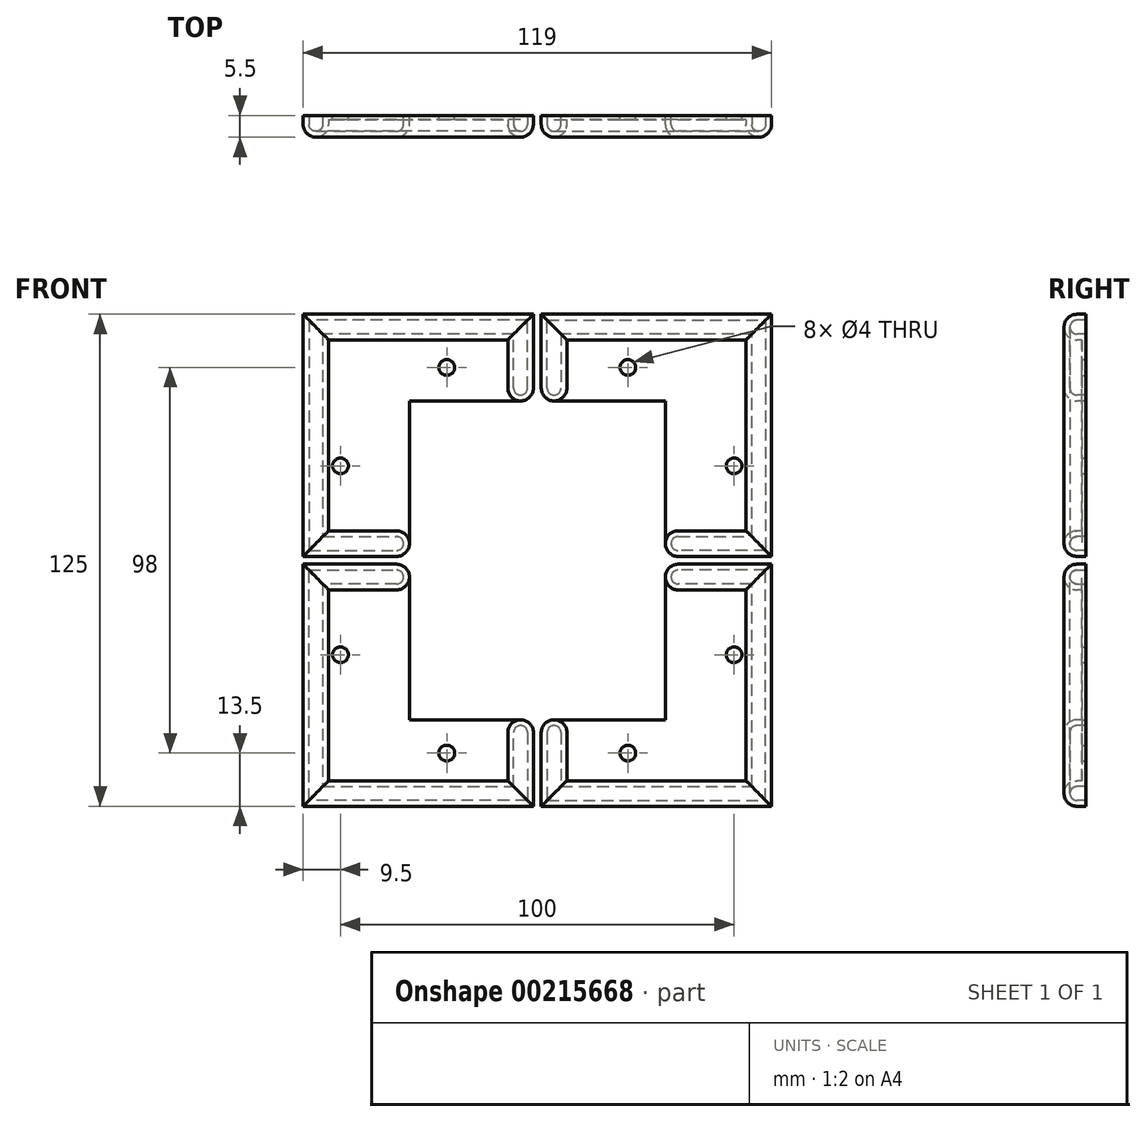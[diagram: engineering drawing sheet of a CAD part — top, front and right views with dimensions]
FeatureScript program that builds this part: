
annotation { "Feature Type Name" : "Feature", "Feature Type Description" : "" }
export const myFeature = defineFeature(function(context is Context, id is Id, definition is map)
    precondition{}
    {
        {
            var Q0;
            Q0=qCreatedBy(makeId("Front.planeOp"),FACE);
            var sketch = newSketch(context, id + "F0", { "sketchPlane" : qUnion([Q0])});
            skLineSegment(sketch, "E0", {"start": v(59.5, 0) * mm, "end": v(59.5, 61.5) * mm});
            skLineSegment(sketch, "E1", {"start": v(59.5, 61.5) * mm, "end": v(1, 61.5) * mm});
            skLineSegment(sketch, "E2", {"start": v(1, 61.5) * mm, "end": v(1, 39.5) * mm});
            skLineSegment(sketch, "E3", {"start": v(1, 39.5) * mm, "end": v(32.5, 39.5) * mm});
            skLineSegment(sketch, "E4", {"start": v(32.5, 39.5) * mm, "end": v(32.5, 0) * mm});
            skLineSegment(sketch, "E5", {"start": v(32.5, 0) * mm, "end": v(59.5, 0) * mm});
            skCircle(sketch, "E6", {"center": v(23, 48) * mm, "radius": 2 * mm});
            skCircle(sketch, "E7", {"center": v(50, 23) * mm, "radius": 2 * mm});
            skSolve(sketch);
        }
        {
            var Q0;
            Q0=qCreatedBy(makeId("Right.planeOp"),FACE);
            var sketch = newSketch(context, id + "F1", { "sketchPlane" : qUnion([Q0])});
            skArc(sketch, "E8", {"start": v(-2.25, 61.5) * mm, "mid": v(-5.5, 58.25) * mm, "end": v(-2.25, 55) * mm});
            skLineSegment(sketch, "E9", {"start": v(0, 61.5) * mm, "end": v(-2.25, 61.5) * mm});
            skLineSegment(sketch, "E10", {"start": v(-2.25, 55) * mm, "end": v(0, 55) * mm});
            skPoint(sketch, "E11", {"position": v(-5.5, 58.25) * mm});
            skLineSegment(sketch, "E12", {"start": v(0, 55) * mm, "end": v(0, 61.5) * mm});
            skSolve(sketch);
        }
        {
            var Q0;
            Q0=qCreatedBy(makeId("Top.planeOp"),FACE);
            cPlane(context, id + "F2", {"entities" : qUnion([Q0]), "cplaneType" : CPlaneType.OFFSET, "offset" : 39.5 * mm, "width" : 150 * mm, "height" : 150 * mm});
        }
        {
            var Q0;
            Q0=qCreatedBy(id+"F2.planeOp",FACE);
            var sketch = newSketch(context, id + "F3", { "sketchPlane" : qUnion([Q0])});
            skArc(sketch, "E13", {"start": v(1, -2.25) * mm, "mid": v(4.25, -5.5) * mm, "end": v(7.5, -2.25) * mm});
            skPoint(sketch, "E14", {"position": v(4.25, -5.5) * mm});
            skPoint(sketch, "E15", {"position": v(1, -2.25) * mm});
            skLineSegment(sketch, "E16", {"start": v(1, 0) * mm, "end": v(7.5, 0) * mm});
            skLineSegment(sketch, "E17", {"start": v(7.5, -2.25) * mm, "end": v(7.5, 0) * mm});
            skLineSegment(sketch, "E18", {"start": v(1, -2.25) * mm, "end": v(1, 0) * mm});
            skSolve(sketch);
        }
        {
            var Q0;
            Q0=makeQuery(id+"F3.imprint","IMPRINT",FACE,{"disambiguationData":[TD([[makeQuery(id+"F3.imprint","IMPRINT",EDGE,{"derivedFrom":sQuery(id+"F3.wireOp",EDGE,"E13")}),1.0]])]});
            var Q1;
            Q1=sQuery(id+"F0.wireOp",EDGE,"E2");
            var Q2;
            Q2=sQuery(id+"F0.wireOp",EDGE,"E1");
            var Q3;
            Q3=sQuery(id+"F0.wireOp",EDGE,"E0");
            var Q4;
            Q4=sQuery(id+"F0.wireOp",EDGE,"E5");
            sweep(context, id + "F4", {"profiles" : qUnion([Q0]), "path" : qUnion([Q1, Q2, Q3, Q4])});
        }
        {
            var Q0;
            Q0 = qSketchRegion(id + "F0", true);
            extrude(context, id + "F5", {"entities" : qUnion([Q0]), "operationType" : NewBodyOperationType.ADD, "depth" : 1 * mm});
        }
        {
            var Q0;
            Q0=makeQuery(id+"F4.opSweep","CAP_EDGE",EDGE,{"disambiguationData":[OSD([sQuery(id+"F0.wireOp",VERTEX,"E2.end"),sQuery(id+"F3.wireOp",EDGE,"E13")])],"isStart":true});
            var Q1;
            Q1=makeQuery(id+"F4.opSweep","CAP_EDGE",EDGE,{"disambiguationData":[OSD([sQuery(id+"F0.wireOp",VERTEX,"E5.start"),sQuery(id+"F3.wireOp",EDGE,"E13")])],"isStart":false});
            fillet(context, id + "F6", {"entities" : qUnion([Q0, Q1]), "radius" : 3.25 * mm, "tangentPropagation" : true, "allowEdgeOverflow" : false});
        }
        {
            var Q0;
            Q0=makeQuery(id+"F4.opSweep","SWEPT_BODY",BODY,{"disambiguationData":[OSD([sQuery(id+"F0.wireOp",EDGE,"E5"),sQuery(id+"F3.wireOp",EDGE,"E13"),sQuery(id+"F3.wireOp",EDGE,"gyNzIB6L-VOB3-YhDV-Oq0C-YqyF9qzvM0NL"),sQuery(id+"F3.wireOp",EDGE,"E16"),sQuery(id+"F3.wireOp",EDGE,"E17")])]});
            var Q1;
            Q1=qCreatedBy(makeId("Right.planeOp"),FACE);
            mirror(context, id + "F7", {"entities" : qUnion([Q0]), "mirrorPlane" : qUnion([Q1])});
        }
        {
            var Q0;
            Q0=qCreatedBy(makeId("Top.planeOp"),FACE);
            cPlane(context, id + "F8", {"entities" : qUnion([Q0]), "cplaneType" : CPlaneType.OFFSET, "offset" : 1 * mm, "oppositeDirection" : true, "width" : 150 * mm, "height" : 150 * mm});
        }
        {
            var Q0;
            Q0=makeQuery(id+"F4.opSweep","SWEPT_BODY",BODY,{"disambiguationData":[OSD([sQuery(id+"F0.wireOp",EDGE,"E5"),sQuery(id+"F3.wireOp",EDGE,"E13"),sQuery(id+"F3.wireOp",EDGE,"E16"),sQuery(id+"F3.wireOp",EDGE,"E17"),sQuery(id+"F3.wireOp",EDGE,"E18")])]});
            var Q1;
            Q1=makeQuery(id+"F7.opPattern","COPY",BODY,{"derivedFrom":makeQuery(id+"F4.opSweep","SWEPT_BODY",BODY,{"disambiguationData":[OSD([sQuery(id+"F0.wireOp",EDGE,"E5"),sQuery(id+"F3.wireOp",EDGE,"E13"),sQuery(id+"F3.wireOp",EDGE,"E16"),sQuery(id+"F3.wireOp",EDGE,"E17"),sQuery(id+"F3.wireOp",EDGE,"E18")])]}),"instanceName":"1"});
            var Q2;
            Q2=qCreatedBy(id+"F8.planeOp",FACE);
            mirror(context, id + "F9", {"entities" : qUnion([Q0, Q1]), "mirrorPlane" : qUnion([Q2])});
        }
        {
            var Q0;
            {var subQ0=sQuery(id+"F0.wireOp",EDGE,"E2");Q0=makeQuery(id+"F7.opPattern","COPY",FACE,{"derivedFrom":makeQuery(id+"F5.boolean.opBoolean","MERGE",FACE,{"derivedFrom":[makeQuery(id+"F4.opSweep","SWEPT_FACE",FACE,{"disambiguationData":[OSD([subQ0,sQuery(id+"F3.wireOp",EDGE,"E16")])]}),makeQuery(id+"F5.opExtrude","CAP_FACE",FACE,{"disambiguationData":[OSD([sQuery(id+"F0.wireOp",EDGE,"E0"),sQuery(id+"F0.wireOp",EDGE,"E1"),subQ0,sQuery(id+"F0.wireOp",EDGE,"E3"),sQuery(id+"F0.wireOp",EDGE,"E4"),sQuery(id+"F0.wireOp",EDGE,"E5"),sQuery(id+"F0.wireOp",EDGE,"E6"),sQuery(id+"F0.wireOp",EDGE,"E7")])],"isStart":true})]}),"instanceName":"1"});}
            var Q1;
            {var subQ0=sQuery(id+"F0.wireOp",EDGE,"E2");Q1=makeQuery(id+"F9.opPattern","COPY",FACE,{"derivedFrom":makeQuery(id+"F7.opPattern","COPY",FACE,{"derivedFrom":makeQuery(id+"F5.boolean.opBoolean","MERGE",FACE,{"derivedFrom":[makeQuery(id+"F4.opSweep","SWEPT_FACE",FACE,{"disambiguationData":[OSD([subQ0,sQuery(id+"F3.wireOp",EDGE,"E16")])]}),makeQuery(id+"F5.opExtrude","CAP_FACE",FACE,{"disambiguationData":[OSD([sQuery(id+"F0.wireOp",EDGE,"E0"),sQuery(id+"F0.wireOp",EDGE,"E1"),subQ0,sQuery(id+"F0.wireOp",EDGE,"E3"),sQuery(id+"F0.wireOp",EDGE,"E4"),sQuery(id+"F0.wireOp",EDGE,"E5"),sQuery(id+"F0.wireOp",EDGE,"E6"),sQuery(id+"F0.wireOp",EDGE,"E7")])],"isStart":true})]}),"instanceName":"1"}),"instanceName":"1"});}
            var Q2;
            {var subQ0=sQuery(id+"F0.wireOp",EDGE,"E2");Q2=makeQuery(id+"F9.opPattern","COPY",FACE,{"derivedFrom":makeQuery(id+"F5.boolean.opBoolean","MERGE",FACE,{"derivedFrom":[makeQuery(id+"F4.opSweep","SWEPT_FACE",FACE,{"disambiguationData":[OSD([subQ0,sQuery(id+"F3.wireOp",EDGE,"E16")])]}),makeQuery(id+"F5.opExtrude","CAP_FACE",FACE,{"disambiguationData":[OSD([sQuery(id+"F0.wireOp",EDGE,"E0"),sQuery(id+"F0.wireOp",EDGE,"E1"),subQ0,sQuery(id+"F0.wireOp",EDGE,"E3"),sQuery(id+"F0.wireOp",EDGE,"E4"),sQuery(id+"F0.wireOp",EDGE,"E5"),sQuery(id+"F0.wireOp",EDGE,"E6"),sQuery(id+"F0.wireOp",EDGE,"E7")])],"isStart":true})]}),"instanceName":"1"});}
            var Q3;
            {var subQ0=sQuery(id+"F0.wireOp",EDGE,"E2");Q3=makeQuery(id+"F5.boolean.opBoolean","MERGE",FACE,{"derivedFrom":[makeQuery(id+"F4.opSweep","SWEPT_FACE",FACE,{"disambiguationData":[OSD([subQ0,sQuery(id+"F3.wireOp",EDGE,"E16")])]}),makeQuery(id+"F5.opExtrude","CAP_FACE",FACE,{"disambiguationData":[OSD([sQuery(id+"F0.wireOp",EDGE,"E0"),sQuery(id+"F0.wireOp",EDGE,"E1"),subQ0,sQuery(id+"F0.wireOp",EDGE,"E3"),sQuery(id+"F0.wireOp",EDGE,"E4"),sQuery(id+"F0.wireOp",EDGE,"E5"),sQuery(id+"F0.wireOp",EDGE,"E6"),sQuery(id+"F0.wireOp",EDGE,"E7")])],"isStart":true})]});}
            shell(context, id + "F10", {"entities" : qUnion([Q0, Q1, Q2, Q3]), "thickness" : 1.5 * mm});
        }
    });
